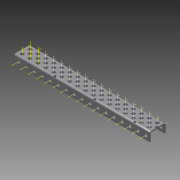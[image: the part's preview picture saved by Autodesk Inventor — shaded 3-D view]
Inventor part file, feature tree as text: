
AUTODESK INVENTOR PART (.ipt)
format: ipt  version: 2015 (Build 190159000, 159)  size: 2,097,152 bytes
history: native  units: in
note: dims shown in document units (in); Inventor stores cm internally (conversion verified against a paired STEP export)
features: other x91, pattern_linear x3, sheet_metal_op x1, extrude x1, imported_body x1, sketch x1
ambient origin geometry x8: Origin, YZ Plane, XZ Plane, XY Plane, X Axis, Y Axis, Z Axis, Center Point
bodies: Body1 (feature_tree)
feature tree (98):
  sheet_metal_op  "Fold1"
  other  "C-Channel"
  extrude  "length cut"  Depth=0.5in
  other  "top axis"
  other  "inner axis"
  other  "front axis"
  other  "back axis"
  pattern_linear  "top axes"  Spacing1=0.5in  [1 undecoded]
  pattern_linear  "inner axes"  Spacing1=0.5in  [1 undecoded]
  pattern_linear  "horiz axes"  Spacing1=-8.5in  [1 undecoded]
  other  "right plane"
  imported_body  "Base1"
  sketch  "Sketch1"  dims[d1=0.0in d4=0.5in d5=0.7874in d7=0.5in d10=0.5in d13=0.5in d14=-8.5in d15=0.0in d16=0.0in d17=0.0in d18=0.0in d19=0.0in]
  other  "Work Point1"
  other  "Work Point2"
  other  "Work Point3"
  other  "Work Point4"
  other  "Work Axis5"
  other  "Work Axis6"
  other  "Work Axis7"
  other  "Work Axis8"
  other  "Work Axis11"
  other  "Work Axis12"
  other  "Work Axis13"
  other  "Work Axis14"
  other  "Work Axis15"
  other  "Work Axis18"
  other  "Work Axis19"
  other  "Work Axis20"
  other  "Work Axis23"
  other  "Work Axis24"
  other  "Work Axis25"
  other  "Work Axis26"
  other  "Work Axis30"
  other  "Work Axis31"
  other  "Work Axis32"
  other  "Work Axis33"
  other  "left plane"
  other  "Work Axis37"
  other  "Work Axis38"
  other  "Work Axis39"
  other  "Work Axis40"
  other  "Work Axis41"
  other  "Work Axis42"
  other  "Work Axis43"
  other  "Work Axis44"
  other  "Work Axis45"
  other  "Work Axis46"
  other  "Work Axis57"
  other  "Work Axis58"
  other  "Work Axis59"
  other  "Work Axis60"
  other  "Work Axis61"
  other  "Work Axis62"
  other  "Work Axis63"
  other  "Work Axis64"
  other  "Work Axis65"
  other  "Work Axis66"
  other  "Work Axis77"
  other  "Work Axis78"
  other  "Work Axis79"
  other  "Work Axis80"
  other  "Work Axis81"
  other  "Work Axis82"
  other  "Work Axis83"
  other  "Work Axis84"
  other  "Work Axis85"
  other  "Work Axis86"
  other  "Work Axis97"
  other  "Work Axis98"
  other  "Work Axis99"
  other  "Work Axis100"
  other  "Work Axis101"
  other  "Work Axis102"
  other  "Work Axis103"
  other  "Work Axis104"
  other  "Work Axis105"
  other  "Work Axis106"
  other  "Work Axis117"
  other  "Work Axis118"
  other  "Work Axis119"
  other  "Work Axis120"
  other  "Work Axis121"
  other  "Work Axis122"
  other  "Work Axis123"
  other  "Work Axis124"
  other  "Work Axis125"
  other  "Work Axis126"
  other  "Work Axis137"
  other  "Work Axis138"
  other  "Work Axis140"
  other  "Work Axis141"
  other  "Work Axis143"
  other  "Work Axis144"
  other  "Work Axis146"
  other  "Work Axis147"
  other  "Work Axis149"
  other  "Work Axis150"
note: 3 required parameter values undecoded (feature->parameter linkage not recoverable at this tier; creation-order binding heuristic only, values carry confidence <= 0.55)
